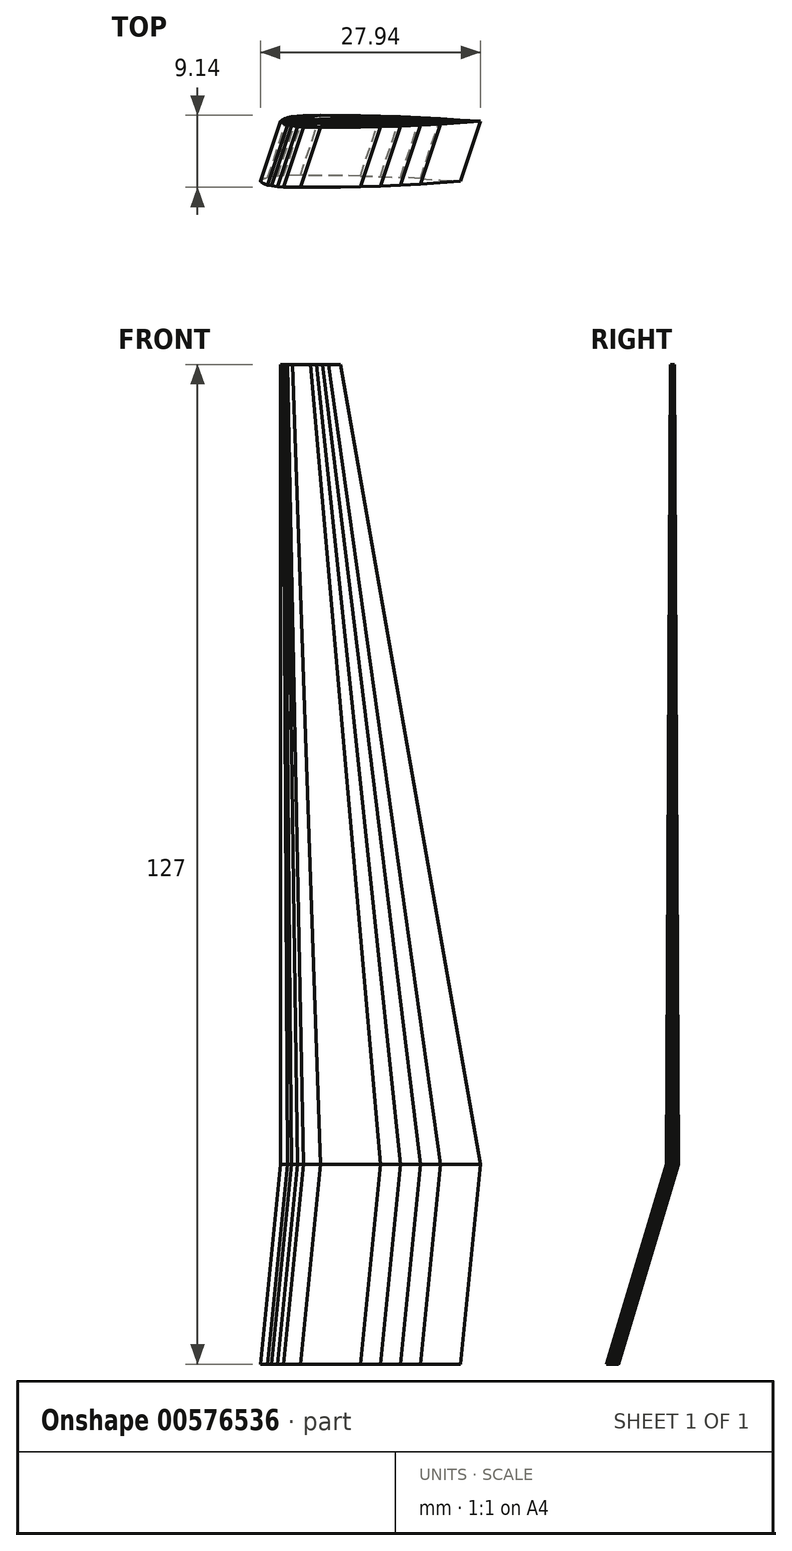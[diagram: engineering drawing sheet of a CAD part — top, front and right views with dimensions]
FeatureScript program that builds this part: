
annotation { "Feature Type Name" : "Feature", "Feature Type Description" : "" }
export const myFeature = defineFeature(function(context is Context, id is Id, definition is map)
    precondition{}
    {
        {
            var Q0;
            Q0=qCreatedBy(makeId("Top.planeOp"),FACE);
            var sketch = newSketch(context, id + "F0", { "sketchPlane" : qUnion([Q0])});
            skPoint(sketch, "E0", {"position": v(0, 0) * mm});
            skPoint(sketch, "E1", {"position": v(2.93, 0.71) * mm});
            skPoint(sketch, "E2", {"position": v(5.06, 0.76) * mm});
            skPoint(sketch, "E3", {"position": v(7.62, 0.73) * mm});
            skPoint(sketch, "E4", {"position": v(10.14, 0.71) * mm});
            skPoint(sketch, "E5", {"position": v(12.7, 0.67) * mm});
            skPoint(sketch, "E6", {"position": v(15.22, 0.6) * mm});
            skPoint(sketch, "E7", {"position": v(17.78, 0.5) * mm});
            skPoint(sketch, "E8", {"position": v(20.29, 0.34) * mm});
            skPoint(sketch, "E9", {"position": v(22.82, 0.17) * mm});
            skPoint(sketch, "E10", {"position": v(25.4, 0) * mm});
            skLineSegment(sketch, "E11", {"start": v(22.82, 0.17) * mm, "end": v(25.4, 0) * mm});
            skLineSegment(sketch, "E12", {"start": v(20.29, 0.34) * mm, "end": v(22.82, 0.17) * mm});
            skLineSegment(sketch, "E13", {"start": v(20.29, 0.34) * mm, "end": v(17.78, 0.5) * mm});
            skLineSegment(sketch, "E14", {"start": v(15.22, 0.6) * mm, "end": v(17.78, 0.5) * mm});
            skLineSegment(sketch, "E15", {"start": v(12.7, 0.67) * mm, "end": v(15.22, 0.6) * mm});
            skLineSegment(sketch, "E16", {"start": v(12.7, 0.67) * mm, "end": v(10.14, 0.71) * mm});
            skLineSegment(sketch, "E17", {"start": v(10.14, 0.71) * mm, "end": v(7.62, 0.73) * mm});
            skLineSegment(sketch, "E18", {"start": v(7.62, 0.73) * mm, "end": v(5.06, 0.76) * mm});
            skLineSegment(sketch, "E19", {"start": v(5.06, 0.76) * mm, "end": v(2.93, 0.71) * mm});
            skLineSegment(sketch, "E20", {"start": v(2.93, 0.71) * mm, "end": v(2.14, 0.65) * mm});
            skLineSegment(sketch, "E21", {"start": v(2.14, 0.65) * mm, "end": v(1.37, 0.57) * mm});
            skLineSegment(sketch, "E22", {"start": v(1.37, 0.57) * mm, "end": v(0.89, 0.47) * mm});
            skLineSegment(sketch, "E23", {"start": v(0.89, 0.47) * mm, "end": v(0.54, 0.34) * mm});
            skArc(sketch, "E24", {"start": v(0.54, 0.34) * mm, "mid": v(0.25, 0.2) * mm, "end": v(0, 0) * mm});
            skLineSegment(sketch, "E25", {"start": v(0, 0) * mm, "end": v(25.4, 0) * mm, "construction": true});
            skLineSegment(sketch, "E26.MirrorCS", {"start": v(0.89, -0.47) * mm, "end": v(0.54, -0.34) * mm});
            skLineSegment(sketch, "E27.MirrorCS", {"start": v(1.37, -0.57) * mm, "end": v(0.89, -0.47) * mm});
            skArc(sketch, "E28.MirrorCS", {"start": v(0.54, -0.34) * mm, "mid": v(0.25, -0.2) * mm, "end": v(0, 0) * mm});
            skLineSegment(sketch, "E29.MirrorCS", {"start": v(2.93, -0.71) * mm, "end": v(2.14, -0.65) * mm});
            skPoint(sketch, "E30.MirrorP", {"position": v(20.29, -0.35) * mm});
            skPoint(sketch, "E31.MirrorP", {"position": v(22.82, -0.17) * mm});
            skPoint(sketch, "E32.MirrorP", {"position": v(2.93, -0.71) * mm});
            skLineSegment(sketch, "E33.MirrorCS", {"start": v(2.14, -0.65) * mm, "end": v(1.37, -0.57) * mm});
            skPoint(sketch, "E34.MirrorP", {"position": v(5.06, -0.76) * mm});
            skPoint(sketch, "E35.MirrorP", {"position": v(17.78, -0.5) * mm});
            skPoint(sketch, "E36.MirrorP", {"position": v(7.62, -0.73) * mm});
            skPoint(sketch, "E37.MirrorP", {"position": v(12.7, -0.67) * mm});
            skLineSegment(sketch, "E38.MirrorCS", {"start": v(7.62, -0.73) * mm, "end": v(5.06, -0.76) * mm});
            skPoint(sketch, "E39.MirrorP", {"position": v(10.14, -0.71) * mm});
            skLineSegment(sketch, "E40.MirrorCS", {"start": v(5.06, -0.76) * mm, "end": v(2.93, -0.71) * mm});
            skLineSegment(sketch, "E41.MirrorCS", {"start": v(20.29, -0.35) * mm, "end": v(22.82, -0.17) * mm});
            skLineSegment(sketch, "E42.MirrorCS", {"start": v(12.7, -0.67) * mm, "end": v(10.14, -0.71) * mm});
            skPoint(sketch, "E43.MirrorP", {"position": v(15.22, -0.6) * mm});
            skLineSegment(sketch, "E44.MirrorCS", {"start": v(12.7, -0.67) * mm, "end": v(15.22, -0.6) * mm});
            skLineSegment(sketch, "E45.MirrorCS", {"start": v(20.29, -0.35) * mm, "end": v(17.78, -0.5) * mm});
            skLineSegment(sketch, "E46.MirrorCS", {"start": v(15.22, -0.6) * mm, "end": v(17.78, -0.5) * mm});
            skLineSegment(sketch, "E47.MirrorCS", {"start": v(10.14, -0.71) * mm, "end": v(7.62, -0.73) * mm});
            skLineSegment(sketch, "E48.MirrorCS", {"start": v(22.82, -0.17) * mm, "end": v(25.4, 0) * mm});
            skSolve(sketch);
        }
        {
            var Q0;
            Q0=qCreatedBy(makeId("Top.planeOp"),FACE);
            cPlane(context, id + "F1", {"entities" : qUnion([Q0]), "cplaneType" : CPlaneType.OFFSET, "offset" : 25.4 * mm, "width" : 152.4 * mm, "height" : 152.4 * mm});
        }
        {
            var Q0;
            Q0=qCreatedBy(id+"F1.planeOp",FACE);
            var sketch = newSketch(context, id + "F2", { "sketchPlane" : qUnion([Q0])});
            skLineSegment(sketch, "E49.0.0", {"start": v(10.16, 6.89) * mm, "end": v(12.68, 6.9) * mm});
            skLineSegment(sketch, "E49.0.1", {"start": v(12.68, 6.9) * mm, "end": v(15.23, 6.95) * mm});
            skLineSegment(sketch, "E49.0.2", {"start": v(15.23, 6.95) * mm, "end": v(17.76, 7.01) * mm});
            skLineSegment(sketch, "E49.0.3", {"start": v(17.76, 7.01) * mm, "end": v(20.32, 7.12) * mm});
            skLineSegment(sketch, "E49.0.4", {"start": v(20.32, 7.12) * mm, "end": v(22.83, 7.27) * mm});
            skLineSegment(sketch, "E49.0.5", {"start": v(22.83, 7.27) * mm, "end": v(25.36, 7.45) * mm});
            skLineSegment(sketch, "E49.0.6", {"start": v(25.36, 7.45) * mm, "end": v(27.94, 7.62) * mm});
            skLineSegment(sketch, "E49.0.7", {"start": v(27.94, 7.62) * mm, "end": v(25.36, 7.79) * mm});
            skLineSegment(sketch, "E49.0.8", {"start": v(25.36, 7.79) * mm, "end": v(22.83, 7.96) * mm});
            skLineSegment(sketch, "E49.0.9", {"start": v(22.83, 7.96) * mm, "end": v(20.32, 8.12) * mm});
            skLineSegment(sketch, "E49.0.10", {"start": v(20.32, 8.12) * mm, "end": v(17.76, 8.22) * mm});
            skLineSegment(sketch, "E49.0.11", {"start": v(17.76, 8.22) * mm, "end": v(15.23, 8.3) * mm});
            skLineSegment(sketch, "E49.0.12", {"start": v(15.23, 8.3) * mm, "end": v(12.68, 8.33) * mm});
            skLineSegment(sketch, "E49.0.13", {"start": v(12.68, 8.33) * mm, "end": v(10.16, 8.35) * mm});
            skLineSegment(sketch, "E49.0.14", {"start": v(10.16, 8.35) * mm, "end": v(7.6, 8.38) * mm});
            skLineSegment(sketch, "E49.0.15", {"start": v(7.6, 8.38) * mm, "end": v(5.47, 8.33) * mm});
            skLineSegment(sketch, "E49.0.16", {"start": v(5.47, 8.33) * mm, "end": v(4.68, 8.27) * mm});
            skLineSegment(sketch, "E49.0.17", {"start": v(4.68, 8.27) * mm, "end": v(3.91, 8.19) * mm});
            skLineSegment(sketch, "E49.0.18", {"start": v(3.91, 8.19) * mm, "end": v(3.43, 8.09) * mm});
            skLineSegment(sketch, "E49.0.19", {"start": v(3.43, 8.09) * mm, "end": v(3.08, 7.96) * mm});
            skArc(sketch, "E49.0.20", {"start": v(3.08, 7.96) * mm, "mid": v(2.8, 7.82) * mm, "end": v(2.54, 7.62) * mm});
            skArc(sketch, "E49.0.21", {"start": v(2.54, 7.62) * mm, "mid": v(2.8, 7.42) * mm, "end": v(3.08, 7.28) * mm});
            skLineSegment(sketch, "E49.0.22", {"start": v(3.08, 7.28) * mm, "end": v(3.43, 7.15) * mm});
            skLineSegment(sketch, "E49.0.23", {"start": v(3.43, 7.15) * mm, "end": v(3.91, 7.05) * mm});
            skLineSegment(sketch, "E49.0.24", {"start": v(3.91, 7.05) * mm, "end": v(4.68, 6.97) * mm});
            skLineSegment(sketch, "E49.0.25", {"start": v(4.68, 6.97) * mm, "end": v(5.47, 6.9) * mm});
            skLineSegment(sketch, "E49.0.26", {"start": v(5.47, 6.9) * mm, "end": v(7.6, 6.86) * mm});
            skLineSegment(sketch, "E49.0.27", {"start": v(7.6, 6.86) * mm, "end": v(10.16, 6.89) * mm});
            skLineSegment(sketch, "E50", {"start": v(2.54, 7.62) * mm, "end": v(27.94, 7.62) * mm, "construction": true});
            skSolve(sketch);
        }
        {
            var Q0;
            Q0 = qSketchRegion(id + "F0", true);
            var Q1;
            Q1 = qSketchRegion(id + "F2", true);
            loft(context, id + "F3", {"sheetProfilesArray" : [{ "sheetProfileEntities" : qUnion([Q0]) }, { "sheetProfileEntities" : qUnion([Q1]) }]});
        }
        {
            var Q0;
            Q0=qCreatedBy(makeId("Top.planeOp"),FACE);
            cPlane(context, id + "F4", {"entities" : qUnion([Q0]), "cplaneType" : CPlaneType.OFFSET, "offset" : 127 * mm, "width" : 152.4 * mm, "height" : 152.4 * mm});
        }
        {
            var Q0;
            Q0=qCreatedBy(id+"F4.planeOp",FACE);
            var sketch = newSketch(context, id + "F5", { "sketchPlane" : qUnion([Q0])});
            skLineSegment(sketch, "E51.0.0", {"start": v(4.85, 7.4) * mm, "end": v(5.6, 7.4) * mm});
            skLineSegment(sketch, "E51.0.1", {"start": v(5.6, 7.4) * mm, "end": v(6.37, 7.42) * mm});
            skLineSegment(sketch, "E51.0.2", {"start": v(6.37, 7.42) * mm, "end": v(7.13, 7.44) * mm});
            skLineSegment(sketch, "E51.0.3", {"start": v(7.13, 7.44) * mm, "end": v(7.9, 7.47) * mm});
            skLineSegment(sketch, "E51.0.4", {"start": v(7.9, 7.47) * mm, "end": v(8.65, 7.52) * mm});
            skLineSegment(sketch, "E51.0.5", {"start": v(8.65, 7.52) * mm, "end": v(9.41, 7.57) * mm});
            skLineSegment(sketch, "E51.0.6", {"start": v(9.41, 7.57) * mm, "end": v(10.19, 7.62) * mm});
            skLineSegment(sketch, "E51.0.7", {"start": v(10.19, 7.62) * mm, "end": v(9.41, 7.67) * mm});
            skLineSegment(sketch, "E51.0.8", {"start": v(9.41, 7.67) * mm, "end": v(8.65, 7.73) * mm});
            skLineSegment(sketch, "E51.0.9", {"start": v(8.65, 7.73) * mm, "end": v(7.9, 7.77) * mm});
            skLineSegment(sketch, "E51.0.10", {"start": v(7.9, 7.77) * mm, "end": v(7.13, 7.8) * mm});
            skLineSegment(sketch, "E51.0.11", {"start": v(7.13, 7.8) * mm, "end": v(6.37, 7.82) * mm});
            skLineSegment(sketch, "E51.0.12", {"start": v(6.37, 7.82) * mm, "end": v(5.6, 7.84) * mm});
            skLineSegment(sketch, "E51.0.13", {"start": v(5.6, 7.84) * mm, "end": v(4.85, 7.84) * mm});
            skLineSegment(sketch, "E51.0.14", {"start": v(4.85, 7.84) * mm, "end": v(4.08, 7.85) * mm});
            skLineSegment(sketch, "E51.0.15", {"start": v(4.08, 7.85) * mm, "end": v(3.45, 7.84) * mm});
            skLineSegment(sketch, "E51.0.16", {"start": v(3.45, 7.84) * mm, "end": v(3.2, 7.82) * mm});
            skLineSegment(sketch, "E51.0.17", {"start": v(3.2, 7.82) * mm, "end": v(2.98, 7.8) * mm});
            skLineSegment(sketch, "E51.0.18", {"start": v(2.98, 7.8) * mm, "end": v(2.83, 7.76) * mm});
            skLineSegment(sketch, "E51.0.19", {"start": v(2.83, 7.76) * mm, "end": v(2.73, 7.73) * mm});
            skArc(sketch, "E51.0.20", {"start": v(2.73, 7.73) * mm, "mid": v(2.64, 7.68) * mm, "end": v(2.57, 7.62) * mm});
            skArc(sketch, "E51.0.21", {"start": v(2.57, 7.62) * mm, "mid": v(2.64, 7.56) * mm, "end": v(2.73, 7.52) * mm});
            skLineSegment(sketch, "E51.0.22", {"start": v(2.73, 7.52) * mm, "end": v(2.83, 7.48) * mm});
            skLineSegment(sketch, "E51.0.23", {"start": v(2.83, 7.48) * mm, "end": v(2.98, 7.45) * mm});
            skLineSegment(sketch, "E51.0.24", {"start": v(2.98, 7.45) * mm, "end": v(3.2, 7.43) * mm});
            skLineSegment(sketch, "E51.0.25", {"start": v(3.2, 7.43) * mm, "end": v(3.45, 7.4) * mm});
            skLineSegment(sketch, "E51.0.26", {"start": v(3.45, 7.4) * mm, "end": v(4.08, 7.4) * mm});
            skLineSegment(sketch, "E51.0.27", {"start": v(4.08, 7.4) * mm, "end": v(4.85, 7.4) * mm});
            skLineSegment(sketch, "E52", {"start": v(2.57, 7.62) * mm, "end": v(10.19, 7.62) * mm, "construction": true});
            skPoint(sketch, "E53.0", {"position": v(2.54, 7.62) * mm});
            skSolve(sketch);
        }
        {
            var Q1;
            Q1 = qSketchRegion(id + "F5", true);
            var Q2;
            Q2 = qSketchRegion(id + "F2", true);
            loft(context, id + "F6", {"operationType" : NewBodyOperationType.ADD, "sheetProfilesArray" : [{ "sheetProfileEntities" : qUnion([Q1]) }, { "sheetProfileEntities" : qUnion([Q2]) }]});
        }
    });
